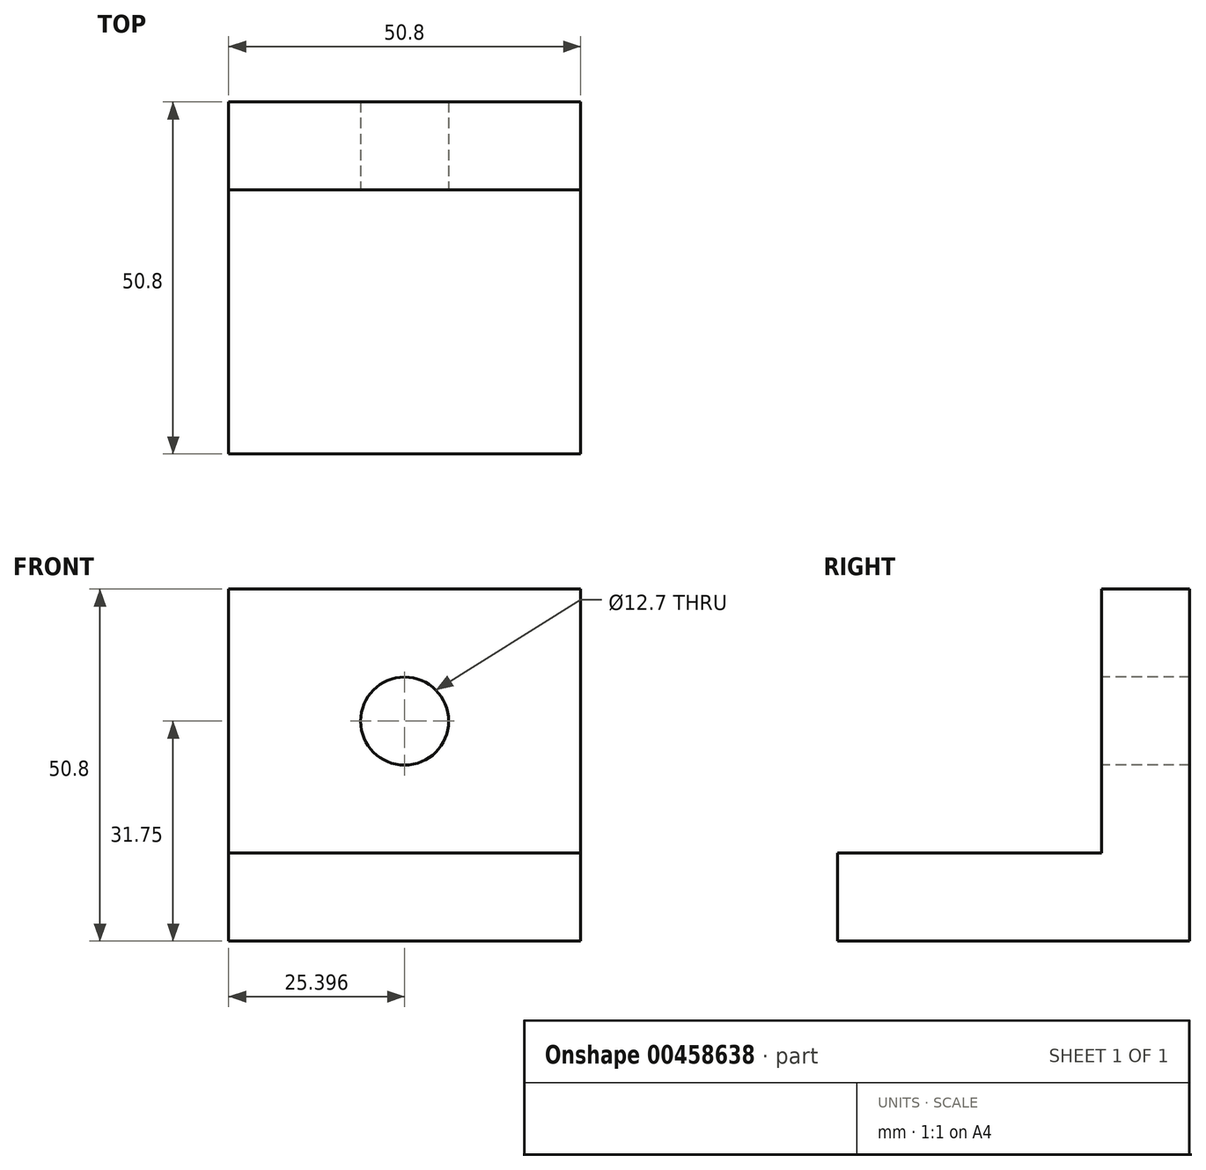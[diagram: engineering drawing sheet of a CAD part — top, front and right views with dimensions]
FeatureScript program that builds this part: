
annotation { "Feature Type Name" : "Feature", "Feature Type Description" : "" }
export const myFeature = defineFeature(function(context is Context, id is Id, definition is map)
    precondition{}
    {
        {
            var Q0;
            Q0=qCreatedBy(makeId("Top.planeOp"),FACE);
            var sketch = newSketch(context, id + "F0", { "sketchPlane" : qUnion([Q0])});
            skLineSegment(sketch, "E0.bottom", {"start": v(-20.2, 29.07) * mm, "end": v(30.6, 29.07) * mm});
            skLineSegment(sketch, "E0.top", {"start": v(-20.2, -21.73) * mm, "end": v(30.6, -21.73) * mm});
            skLineSegment(sketch, "E0.left", {"start": v(-20.2, 29.07) * mm, "end": v(-20.2, -21.73) * mm});
            skLineSegment(sketch, "E0.right", {"start": v(30.6, 29.07) * mm, "end": v(30.6, -21.73) * mm});
            skSolve(sketch);
        }
        {
            var Q0;
            Q0=makeQuery(id+"F0.imprint","IMPRINT",FACE,{"disambiguationData":[TD([[makeQuery(id+"F0.imprint","IMPRINT",EDGE,{"derivedFrom":sQuery(id+"F0.wireOp",EDGE,"E0.bottom")}),-1.0]])]});
            extrude(context, id + "F1", {"entities" : qUnion([Q0]), "depth" : 12.7 * mm});
        }
        {
            var Q0;
            Q0=makeQuery(id+"F1.opExtrude","CAP_FACE",FACE,{"disambiguationData":[OSD([sQuery(id+"F0.wireOp",EDGE,"E0.bottom"),sQuery(id+"F0.wireOp",EDGE,"E0.top"),sQuery(id+"F0.wireOp",EDGE,"E0.left"),sQuery(id+"F0.wireOp",EDGE,"E0.right")])],"isStart":false});
            var sketch = newSketch(context, id + "F2", { "sketchPlane" : qUnion([Q0])});
            skLineSegment(sketch, "E1.bottom", {"start": v(-20.2, 29.07) * mm, "end": v(30.6, 29.07) * mm});
            skLineSegment(sketch, "E1.top", {"start": v(-20.2, 16.37) * mm, "end": v(30.6, 16.37) * mm});
            skLineSegment(sketch, "E1.left", {"start": v(-20.2, 29.07) * mm, "end": v(-20.2, 16.37) * mm});
            skLineSegment(sketch, "E1.right", {"start": v(30.6, 29.07) * mm, "end": v(30.6, 16.37) * mm});
            skSolve(sketch);
        }
        {
            var Q0;
            Q0=makeQuery(id+"F2.imprint","IMPRINT",FACE,{"disambiguationData":[TD([[makeQuery(id+"F2.imprint","IMPRINT",EDGE,{"derivedFrom":sQuery(id+"F2.wireOp",EDGE,"E1.bottom")}),-1.0]])]});
            extrude(context, id + "F3", {"entities" : qUnion([Q0]), "operationType" : NewBodyOperationType.ADD, "depth" : 38.1 * mm});
        }
        {
            var Q0;
            Q0=makeQuery(id+"F3.opExtrude","SWEPT_FACE",FACE,{"disambiguationData":[OSD([sQuery(id+"F2.wireOp",EDGE,"E1.top")])]});
            var sketch = newSketch(context, id + "F4", { "sketchPlane" : qUnion([Q0])});
            skCircle(sketch, "E2", {"center": v(5.2, 31.75) * mm, "radius": 6.35 * mm});
            skPoint(sketch, "E2.centerSnap0", {"position": v(-20.2, 31.75) * mm});
            skPoint(sketch, "E2.centerSnap1", {"position": v(5.2, 50.8) * mm});
            skSolve(sketch);
        }
        {
            var Q0;
            Q0 = qSketchRegion(id + "F4", true);
            extrude(context, id + "F5", {"entities" : qUnion([Q0]), "operationType" : NewBodyOperationType.REMOVE, "oppositeDirection" : true, "depth" : 25.4 * mm});
        }
    });
